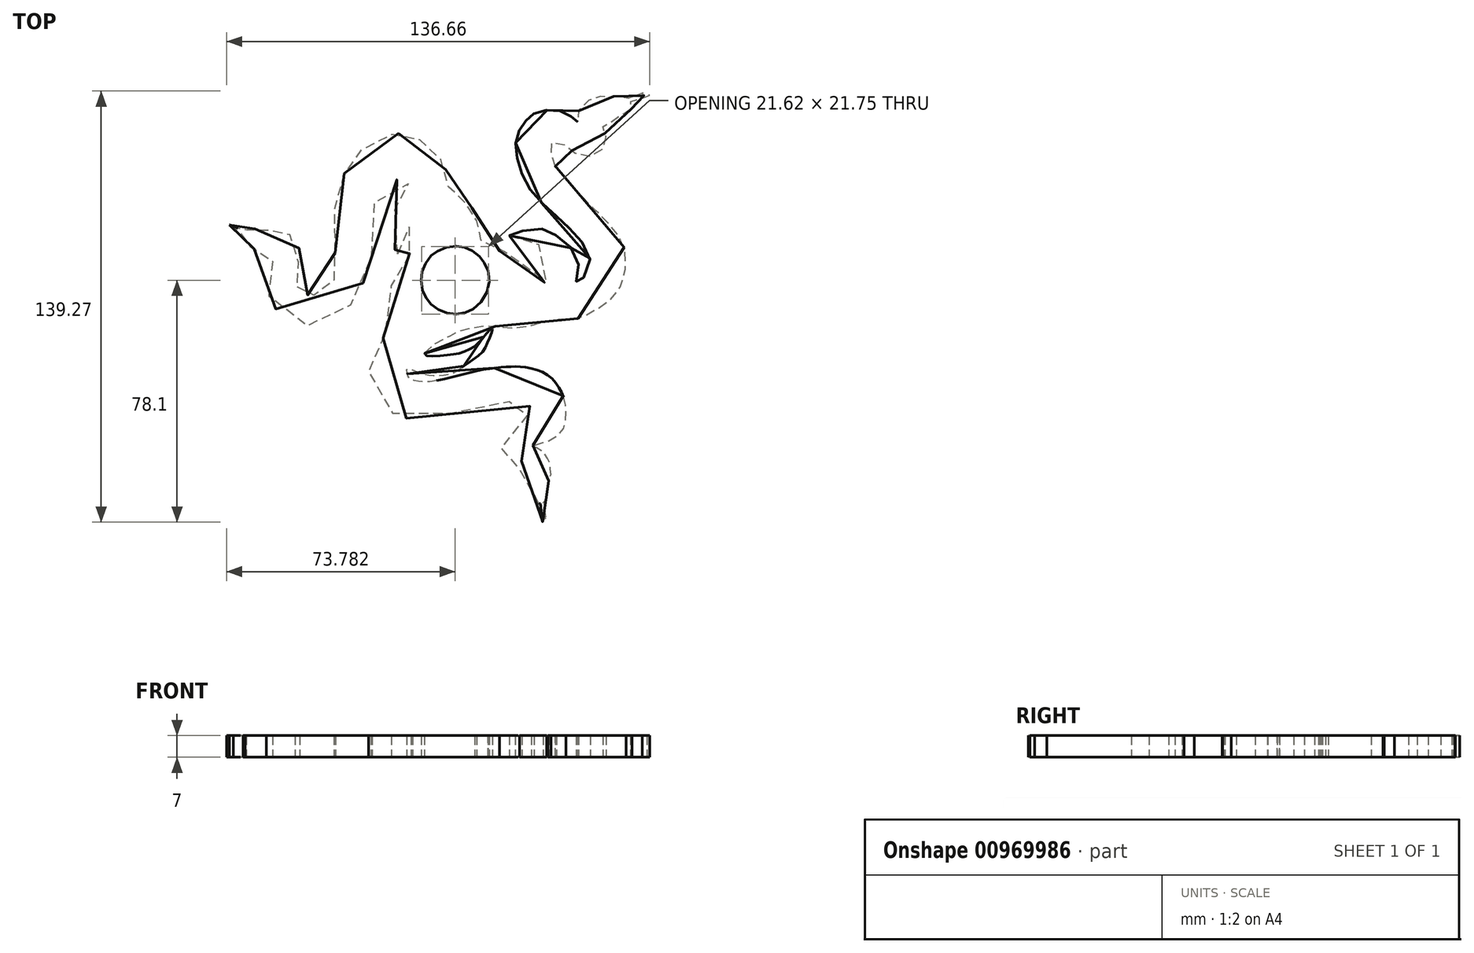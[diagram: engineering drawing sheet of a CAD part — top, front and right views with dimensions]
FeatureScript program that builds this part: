
annotation { "Feature Type Name" : "Feature", "Feature Type Description" : "" }
export const myFeature = defineFeature(function(context is Context, id is Id, definition is map)
    precondition{}
    {
        {
            var Q0;
            Q0=qCreatedBy(makeId("Top.planeOp"),FACE);
            var Q1;
            Q1=qCreatedBy(makeId("Top.planeOp"),FACE);
            var sketch = newSketch(context, id + "F0", { "sketchPlane" : qUnion([Q0, Q1])});
            skPoint(sketch, "E0.88.internal.snap0", {"position": v(62.83, -8.67) * mm});
            skFitSpline(sketch, "E0", {"points": [v(-72.92, 17.83) * mm, v(-71.67, 16.72) * mm, v(-73.8, 16.8) * mm, v(-67.91, 14.7) * mm, v(-68.17, 14.22) * mm, v(-68.34, 13.15) * mm, v(-66.69, 11.29) * mm, v(-62.69, 9.1) * mm, v(-58.93, 6.88) * mm, v(-59.97, 4.35) * mm, v(-60.8, -2.55) * mm, v(-55.11, -12.02) * mm, v(-40.17, -13.91) * mm, v(-31.97, -5.07) * mm, v(-26.92, 8.18) * mm, v(-26.5, 23.75) * mm, v(-18.08, 32.59) * mm, v(-14.3, 29.43) * mm, v(-17.66, 24.8) * mm, v(-20.6, 18.91) * mm, v(-18.5, 7.55) * mm, v(-17.24, 12.81) * mm, v(-14.3, 18.07) * mm, v(-13.87, 18.7) * mm, v(-15.38, 6.03) * mm, v(-18.08, 2.92) * mm, v(-21.66, -5.92) * mm, v(-22.7, -17.49) * mm, v(-27.34, -25.48) * mm, v(-26.29, -35.8) * mm, v(-16.82, -44.42) * mm, v(3.17, -41.68) * mm, v(19.8, -39.37) * mm, v(25.47, -42.1) * mm, v(18.74, -46.1) * mm, v(14.74, -54.1) * mm, v(21.48, -58.52) * mm, v(20.84, -60.83) * mm, v(24.21, -69.46) * mm, v(27.37, -72.2) * mm, v(27.47, -72.17) * mm, v(28.24, -78.16) * mm, v(28.67, -76.17) * mm, v(29.61, -77.66) * mm, v(28.4, -71.9) * mm, v(28.96, -71.34) * mm, v(29.94, -68.9) * mm, v(30.11, -65.14) * mm, v(30.95, -63.28) * mm, v(30.64, -61.25) * mm, v(30.91, -60.16) * mm, v(29.72, -57.38) * mm, v(27.37, -54.59) * mm, v(24.67, -53.7) * mm, v(27.77, -52.73) * mm, v(34.23, -49.24) * mm, v(35.73, -44.55) * mm, v(35.75, -41.1) * mm, v(34.52, -36.58) * mm, v(29.72, -30.56) * mm, v(21.7, -28.05) * mm, v(16.2, -28.05) * mm, v(6.45, -29.46) * mm, v(-8.65, -32.81) * mm, v(-14.45, -31.92) * mm, v(-15.27, -30.65) * mm, v(-15.42, -28.57) * mm, v(-12.22, -29.69) * mm, v(-8.87, -30.58) * mm, v(-1.95, -30.36) * mm, v(3.63, -27.16) * mm, v(8.5, -23.5) * mm, v(10.43, -20.34) * mm, v(11.88, -16.55) * mm, v(11.88, -15.6) * mm, v(8.93, -18.65) * mm, v(6.09, -21.5) * mm, v(1.78, -23.49) * mm, v(-2.96, -24.23) * mm, v(-9.38, -24.33) * mm, v(-9.59, -22.86) * mm, v(-0.85, -17.6) * mm, v(1.3, -16.47) * mm, v(9.25, -14.76) * mm, v(15.45, -15.28) * mm, v(24.4, -14.76) * mm, v(31.44, -12.76) * mm, v(39.33, -12.44) * mm, v(46.8, -8.67) * mm, v(52.8, -3.3) * mm, v(55.05, 8.59) * mm, v(50.54, 17.22) * mm, v(42.29, 25.6) * mm, v(32.7, 36.45) * mm], "startDerivative": vector(405.88, -255.22) * mm, "endDerivative": vector(-559.52, 661.11) * mm});
            skFitSpline(sketch, "E1", {"points": [v(32.4, 36.75) * mm, v(31.13, 40.54) * mm, v(31.06, 44.33) * mm, v(35.97, 43.51) * mm, v(38.87, 40.99) * mm, v(45.49, 40.46) * mm, v(48.61, 44.1) * mm, v(48.46, 47.3) * mm, v(47.77, 49.72) * mm, v(49, 50.24) * mm, v(50.93, 51.73) * mm, v(55.65, 54.37) * mm, v(57.16, 56.11) * mm, v(56.72, 57.67) * mm, v(59.35, 58.46) * mm, v(61.22, 59.24) * mm, v(62.83, 59.74) * mm, v(60.47, 59.8) * mm, v(61.94, 61.1) * mm, v(56.12, 58.61) * mm, v(55.62, 59.08) * mm, v(51.4, 59.4) * mm, v(50.56, 59.02) * mm, v(48.4, 59.18) * mm, v(46.3, 59.33) * mm, v(42.05, 57.36) * mm, v(39.48, 53.2) * mm, v(39.6, 50.98) * mm, v(36.98, 53.3) * mm, v(32.73, 54.9) * mm, v(26.57, 54.36) * mm, v(23.56, 52.23) * mm, v(21.19, 49.33) * mm, v(19.5, 44.18) * mm, v(20.56, 37.44) * mm, v(24.35, 29.13) * mm, v(32.08, 21.24) * mm, v(38.98, 14.7) * mm, v(43.5, 4.81) * mm, v(39.3, -0.87) * mm, v(39.82, 6.03) * mm, v(32.7, 14.38) * mm, v(25.72, 16.6) * mm, v(17.52, 14.38) * mm, v(25.2, 13.12) * mm, v(29.5, 1.02) * mm, v(28.04, -0.98) * mm, v(22.56, 5.02) * mm, v(15.94, 9.23) * mm, v(13.4, 9.67) * mm, v(6.4, 15.23) * mm, v(7, 17.96) * mm, v(5.1, 23.75) * mm, v(2.47, 25.6) * mm, v(-1.53, 28.27) * mm, v(-2.58, 33.74) * mm, v(-5.84, 40.68) * mm, v(-11.52, 45.42) * mm, v(-18.15, 47.42) * mm, v(-28.69, 43.23) * mm, v(-33.46, 38.63) * mm, v(-38.15, 28.1) * mm, v(-39.13, 16.78) * mm, v(-38.68, 3.87) * mm, v(-40.37, -2.12) * mm, v(-45.77, -4.86) * mm, v(-48.95, -4.24) * mm, v(-51.43, -1.41) * mm, v(-50.99, 4.16) * mm, v(-50.81, 11.5) * mm, v(-56.83, 16.46) * mm, v(-59.66, 16.01) * mm, v(-63.1, 16.55) * mm, v(-67.53, 16.01) * mm, v(-67.47, 15.54) * mm, v(-67.77, 15.63) * mm, v(-69.7, 16.4) * mm, v(-71.28, 17.34) * mm, v(-72.4, 17.72) * mm, v(-72.92, 17.83) * mm], "startDerivative": vector(-105.54, 296.9) * mm, "endDerivative": vector(-108.75, 20.78) * mm});
            skFitSpline(sketch, "E2", {"points": [v(32.37, 36.77) * mm, v(32.75, 36.37) * mm, v(32.73, 36.44) * mm, v(32.37, 36.77) * mm]});
            skFitSpline(sketch, "E3", {"points": [v(32.7, 36.45) * mm, v(32.4, 36.74) * mm], "startDerivative": vector(-0.3, 0.3) * mm, "endDerivative": vector(-0.3, 0.3) * mm});
            skFitSpline(sketch, "E4", {"points": [v(10.78, 2.19) * mm, v(10.96, -0.88) * mm, v(9.26, -5.94) * mm, v(5.8, -9.35) * mm, v(2.68, -10.67) * mm, v(-1, -10.95) * mm, v(-4.78, -9.9) * mm, v(-7.6, -7.95) * mm, v(-9.43, -5.66) * mm, v(-10.66, -2.72) * mm, v(-10.9, 1.42) * mm, v(-10.17, 4.18) * mm, v(-7.93, 7.62) * mm, v(-6.1, 9.15) * mm, v(-2.3, 10.76) * mm, v(1.6, 10.88) * mm, v(4.45, 10.06) * mm, v(7.42, 8.12) * mm, v(9.2, 6.03) * mm, v(10.59, 2.98) * mm], "startDerivative": vector(9.3, -57.88) * mm, "endDerivative": vector(25.37, -63.4) * mm});
            skFitSpline(sketch, "E5", {"points": [v(10.78, 2.19) * mm, v(10.6, 2.97) * mm], "startDerivative": vector(-0.18, 0.79) * mm, "endDerivative": vector(-0.18, 0.79) * mm});
            skFitSpline(sketch, "E6", {"points": [v(10.78, 2.19) * mm, v(10.78, 2.19) * mm], "startDerivative": vector(0, 0) * mm, "endDerivative": vector(0, 0) * mm});
            skFitSpline(sketch, "E7", {"points": [v(10.6, 2.97) * mm, v(10.59, 2.98) * mm], "startDerivative": vector(0, 0) * mm, "endDerivative": vector(0, 0) * mm});
            skSolve(sketch);
        }
        {
            var Q0;
            {var subQ0=sQuery(id+"F0.wireOp",EDGE,"E1");var subQ1=sQuery(id+"F0.wireOp",EDGE,"E0");var subQ2=makeQuery(id+"F0.imprint","INTERSECT",VERTEX,{"derivedFrom":[subQ1,subQ0]});Q0=makeQuery(id+"F0.imprint","IMPRINT",FACE,{"disambiguationData":[TD([[makeQuery(id+"F0.imprint","IMPRINT",EDGE,{"disambiguationData":[TD([[subQ2,-1.0]])],"derivedFrom":subQ1}),1.0]])]});}
            var Q1;
            Q1=makeQuery(id+"F0.imprint","IMPRINT",FACE,{"disambiguationData":[TD([[makeQuery(id+"F0.imprint","IMPRINT",EDGE,{"derivedFrom":sQuery(id+"F0.wireOp",EDGE,"E4")}),1.0]])]});
            extrude(context, id + "F1", {"entities" : qUnion([Q0, Q1]), "depth" : 7 * mm, "offsetDistance" : 25 * mm});
        }
    });
